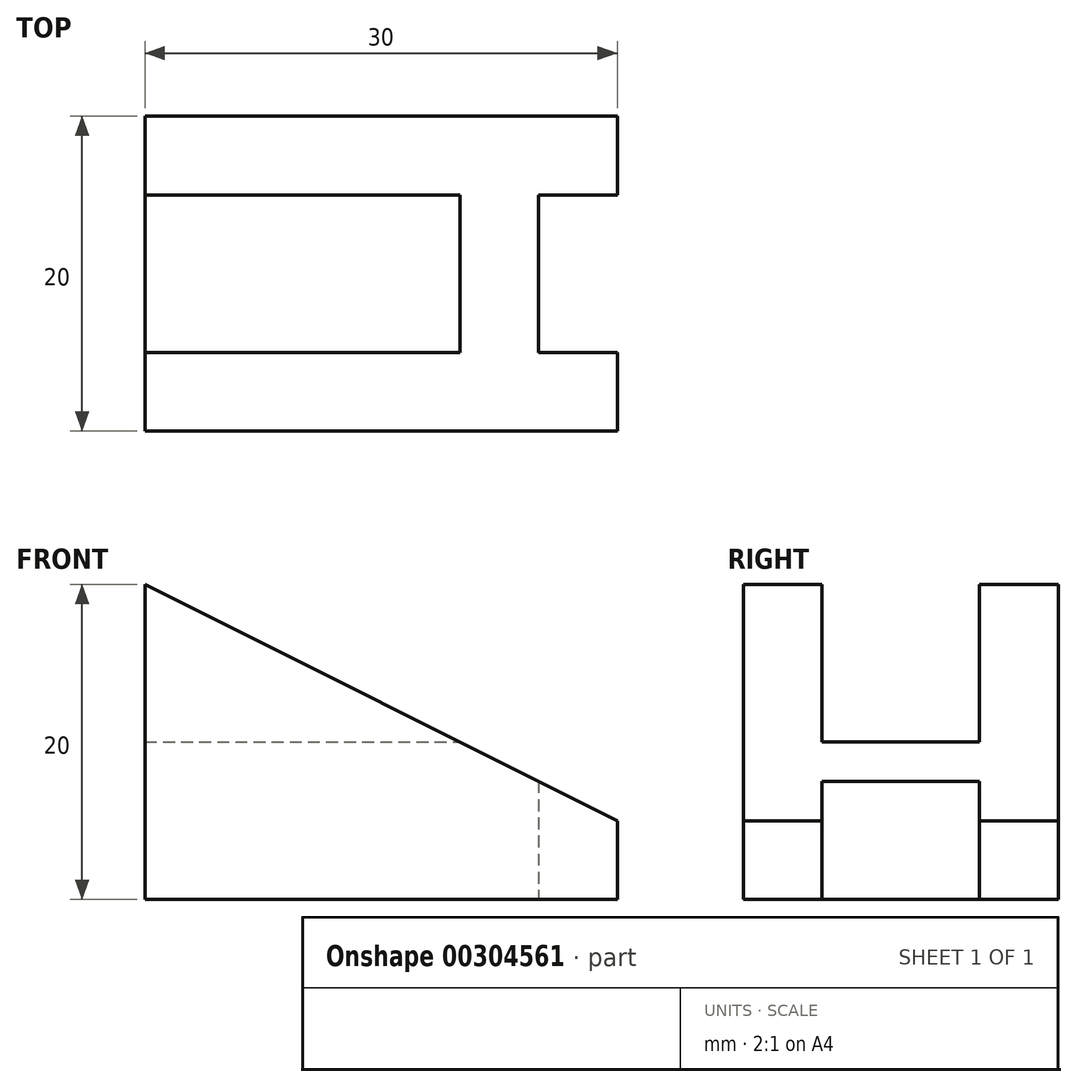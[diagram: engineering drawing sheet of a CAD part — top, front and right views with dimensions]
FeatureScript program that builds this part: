
annotation { "Feature Type Name" : "Feature", "Feature Type Description" : "" }
export const myFeature = defineFeature(function(context is Context, id is Id, definition is map)
    precondition{}
    {
        {
            var Q0;
            Q0=qCreatedBy(makeId("Front.planeOp"),FACE);
            var sketch = newSketch(context, id + "F0", { "sketchPlane" : qUnion([Q0])});
            skLineSegment(sketch, "E0", {"start": v(0, 0) * mm, "end": v(0, 20) * mm});
            skLineSegment(sketch, "E1", {"start": v(30, 0) * mm, "end": v(0, 0) * mm});
            skLineSegment(sketch, "E2", {"start": v(30, 0) * mm, "end": v(30, 5) * mm});
            skLineSegment(sketch, "E3", {"start": v(30, 5) * mm, "end": v(0, 20) * mm});
            skSolve(sketch);
        }
        {
            var Q0;
            Q0=makeQuery(id+"F0.imprint","IMPRINT",FACE,{"disambiguationData":[TD([[makeQuery(id+"F0.imprint","IMPRINT",EDGE,{"derivedFrom":sQuery(id+"F0.wireOp",EDGE,"E0")}),-1.0]])]});
            extrude(context, id + "F1", {"entities" : qUnion([Q0]), "depth" : 20 * mm, "symmetric" : true});
        }
        {
            var Q0;
            Q0=makeQuery(id+"F1.opExtrude","CAP_FACE",FACE,{"disambiguationData":[OSD([sQuery(id+"F0.wireOp",EDGE,"E0"),sQuery(id+"F0.wireOp",EDGE,"a0i82NZJ-huY0-82R9-GRY0-XSOW82q7UUxD"),sQuery(id+"F0.wireOp",EDGE,"E1")])],"isStart":false});
            var sketch = newSketch(context, id + "F2", { "sketchPlane" : qUnion([Q0])});
            skLineSegment(sketch, "E4", {"start": v(0, 20) * mm, "end": v(0, 10) * mm});
            skLineSegment(sketch, "E5", {"start": v(0, 10) * mm, "end": v(20, 10) * mm});
            skLineSegment(sketch, "E6", {"start": v(20, 10) * mm, "end": v(0, 20) * mm});
            skSolve(sketch);
        }
        {
            var Q0;
            Q0=makeQuery(id+"F2.imprint","IMPRINT",FACE,{"disambiguationData":[TD([[makeQuery(id+"F2.imprint","IMPRINT",EDGE,{"derivedFrom":sQuery(id+"F2.wireOp",EDGE,"E4")}),-1.0]])]});
            extrude(context, id + "F3", {"entities" : qUnion([Q0]), "operationType" : NewBodyOperationType.REMOVE, "oppositeDirection" : true, "depth" : 15 * mm, "hasSecondDirection" : true, "secondDirectionOppositeDirection" : true, "secondDirectionDepth" : 5 * mm});
        }
        {
            var Q0;
            Q0=makeQuery(id+"F1.opExtrude","CAP_FACE",FACE,{"disambiguationData":[OSD([sQuery(id+"F0.wireOp",EDGE,"E0"),sQuery(id+"F0.wireOp",EDGE,"E1"),sQuery(id+"F0.wireOp",EDGE,"E2"),sQuery(id+"F0.wireOp",EDGE,"E3")])],"isStart":false});
            var sketch = newSketch(context, id + "F4", { "sketchPlane" : qUnion([Q0])});
            skLineSegment(sketch, "E7", {"start": v(25, 7.5) * mm, "end": v(25, 0) * mm});
            skLineSegment(sketch, "E8", {"start": v(25, 0) * mm, "end": v(30, 0) * mm});
            skLineSegment(sketch, "E9", {"start": v(30, 0) * mm, "end": v(30, 5) * mm});
            skLineSegment(sketch, "E10", {"start": v(30, 5) * mm, "end": v(25, 7.5) * mm});
            skSolve(sketch);
        }
        {
            var Q0;
            Q0=makeQuery(id+"F4.imprint","IMPRINT",FACE,{"disambiguationData":[TD([[makeQuery(id+"F4.imprint","IMPRINT",EDGE,{"derivedFrom":sQuery(id+"F4.wireOp",EDGE,"E7")}),1.0]])]});
            extrude(context, id + "F5", {"entities" : qUnion([Q0]), "operationType" : NewBodyOperationType.REMOVE, "oppositeDirection" : true, "depth" : 15 * mm, "hasSecondDirection" : true, "secondDirectionOppositeDirection" : true, "secondDirectionDepth" : 5 * mm});
        }
    });
